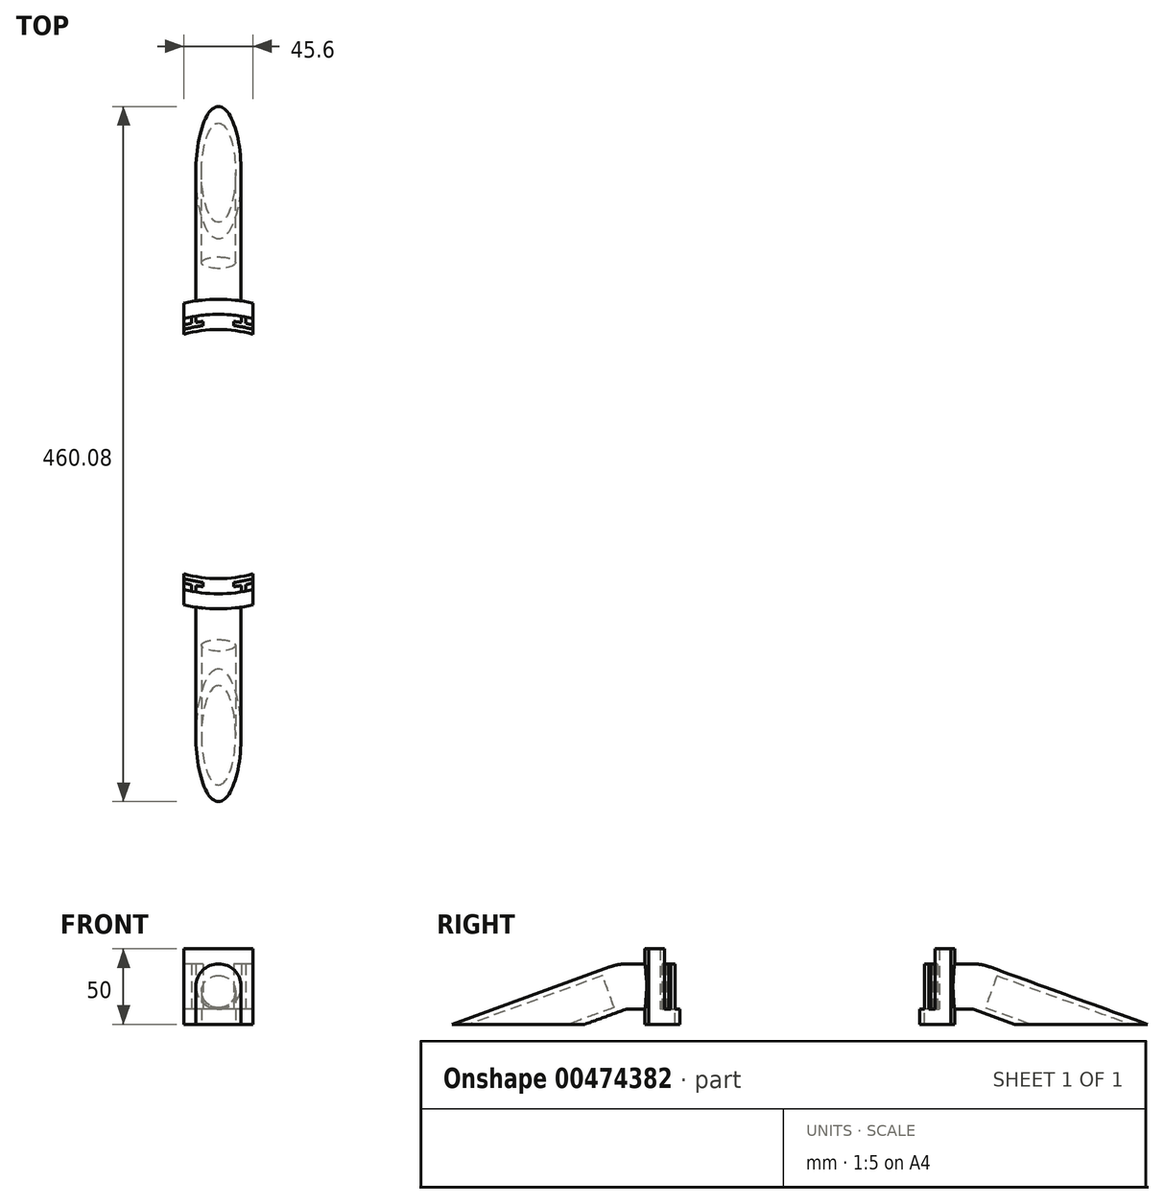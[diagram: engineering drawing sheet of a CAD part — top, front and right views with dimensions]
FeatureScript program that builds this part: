
annotation { "Feature Type Name" : "Feature", "Feature Type Description" : "" }
export const myFeature = defineFeature(function(context is Context, id is Id, definition is map)
    precondition{}
    {
        {
            var Q0;
            Q0=qCreatedBy(makeId("Top.planeOp"),FACE);
            var sketch = newSketch(context, id + "F0", { "sketchPlane" : qUnion([Q0])});
            skArc(sketch, "E0", {"start": v(-15.1, 91.26) * mm, "mid": v(-16.5, 91.02) * mm, "end": v(-17.9, 90.75) * mm});
            skCircle(sketch, "E1", {"center": v(0, 0) * mm, "radius": 82.5 * mm, "construction": true});
            skLineSegment(sketch, "E2", {"start": v(0, 0) * mm, "end": v(0, 99.1) * mm, "construction": true});
            skArc(sketch, "E3", {"start": v(-17.9, 86.57) * mm, "mid": v(-20.36, 86.02) * mm, "end": v(-22.8, 85.4) * mm});
            skArc(sketch, "E4", {"start": v(-10.2, 85) * mm, "mid": v(-16.54, 83.99) * mm, "end": v(-22.8, 82.5) * mm});
            skLineSegment(sketch, "E5", {"start": v(-15.1, 87.1) * mm, "end": v(-15.1, 91.26) * mm});
            skLineSegment(sketch, "E6", {"start": v(-17.9, 86.57) * mm, "end": v(-17.9, 90.75) * mm});
            skLineSegment(sketch, "E7", {"start": v(-10.2, 87.8) * mm, "end": v(-10.2, 85) * mm});
            skLineSegment(sketch, "E8", {"start": v(-22.8, 85.4) * mm, "end": v(-22.8, 82.5) * mm});
            skLineSegment(sketch, "E9.MirrorCS", {"start": v(10.2, 87.8) * mm, "end": v(10.2, 85) * mm});
            skLineSegment(sketch, "E10.MirrorCS", {"start": v(15.1, 87.1) * mm, "end": v(15.1, 91.26) * mm});
            skLineSegment(sketch, "E11.MirrorCS", {"start": v(17.9, 86.57) * mm, "end": v(17.9, 90.75) * mm});
            skLineSegment(sketch, "E12.MirrorCS", {"start": v(22.8, 85.4) * mm, "end": v(22.8, 82.5) * mm});
            skArc(sketch, "E13.trimOffspring", {"start": v(-10.2, 87.8) * mm, "mid": v(-12.65, 87.49) * mm, "end": v(-15.1, 87.1) * mm});
            skArc(sketch, "E14.trimOffspring", {"start": v(15.1, 87.1) * mm, "mid": v(12.65, 87.49) * mm, "end": v(10.2, 87.8) * mm});
            skArc(sketch, "E15.trimOffspring", {"start": v(17.9, 90.75) * mm, "mid": v(16.5, 91.02) * mm, "end": v(15.1, 91.26) * mm});
            skArc(sketch, "E16.trimOffspring", {"start": v(22.8, 82.5) * mm, "mid": v(16.54, 83.99) * mm, "end": v(10.2, 85) * mm});
            skArc(sketch, "E17.trimOffspring", {"start": v(22.8, 85.4) * mm, "mid": v(20.36, 86.02) * mm, "end": v(17.9, 86.57) * mm});
            skLineSegment(sketch, "E18", {"start": v(-16.5, 91.02) * mm, "end": v(-16.5, 84) * mm, "construction": true});
            skLineSegment(sketch, "E19", {"start": v(16.5, 91.02) * mm, "end": v(16.5, 84) * mm, "construction": true});
            skArc(sketch, "E20.1.0", {"start": v(10.2, -85) * mm, "mid": v(16.54, -83.99) * mm, "end": v(22.8, -82.5) * mm});
            skLineSegment(sketch, "E20.1.1", {"start": v(22.8, -85.4) * mm, "end": v(22.8, -82.5) * mm});
            skArc(sketch, "E20.1.2", {"start": v(17.9, -86.57) * mm, "mid": v(20.36, -86.02) * mm, "end": v(22.8, -85.4) * mm});
            skLineSegment(sketch, "E20.1.3", {"start": v(17.9, -86.57) * mm, "end": v(17.9, -90.75) * mm});
            skArc(sketch, "E20.1.4", {"start": v(15.1, -91.26) * mm, "mid": v(16.5, -91.02) * mm, "end": v(17.9, -90.75) * mm});
            skLineSegment(sketch, "E20.1.5", {"start": v(15.1, -87.1) * mm, "end": v(15.1, -91.26) * mm});
            skArc(sketch, "E20.1.6", {"start": v(10.2, -87.8) * mm, "mid": v(12.65, -87.49) * mm, "end": v(15.1, -87.1) * mm});
            skLineSegment(sketch, "E20.1.7", {"start": v(10.2, -87.8) * mm, "end": v(10.2, -85) * mm});
            skArc(sketch, "E20.1.8", {"start": v(-22.8, -82.5) * mm, "mid": v(-16.54, -83.99) * mm, "end": v(-10.2, -85) * mm});
            skLineSegment(sketch, "E20.1.9", {"start": v(-10.2, -87.8) * mm, "end": v(-10.2, -85) * mm});
            skArc(sketch, "E20.1.10", {"start": v(-15.1, -87.1) * mm, "mid": v(-12.65, -87.49) * mm, "end": v(-10.2, -87.8) * mm});
            skLineSegment(sketch, "E20.1.11", {"start": v(-15.1, -87.1) * mm, "end": v(-15.1, -91.26) * mm});
            skArc(sketch, "E20.1.12", {"start": v(-17.9, -90.75) * mm, "mid": v(-16.5, -91.02) * mm, "end": v(-15.1, -91.26) * mm});
            skLineSegment(sketch, "E20.1.13", {"start": v(-17.9, -86.57) * mm, "end": v(-17.9, -90.75) * mm});
            skArc(sketch, "E20.1.14", {"start": v(-22.8, -85.4) * mm, "mid": v(-20.36, -86.02) * mm, "end": v(-17.9, -86.57) * mm});
            skLineSegment(sketch, "E20.1.15", {"start": v(-22.8, -85.4) * mm, "end": v(-22.8, -82.5) * mm});
            skSolve(sketch);
        }
        {
            var Q0;
            Q0 = qSketchRegion(id + "F0", true);
            extrude(context, id + "F1", {"entities" : qUnion([Q0]), "depth" : 30 * mm});
        }
        {
            var Q0;
            Q0=qCreatedBy(makeId("Top.planeOp"),FACE);
            var sketch = newSketch(context, id + "F2", { "sketchPlane" : qUnion([Q0])});
            skArc(sketch, "E21", {"start": v(22.8, 89.65) * mm, "mid": v(0, 92.5) * mm, "end": v(-22.8, 89.65) * mm});
            skArc(sketch, "E22", {"start": v(22.8, 79.29) * mm, "mid": v(0, 82.5) * mm, "end": v(-22.8, 79.29) * mm});
            skArc(sketch, "E23.0.4", {"start": v(-15.1, 91.26) * mm, "mid": v(-16.5, 91.02) * mm, "end": v(-17.9, 90.75) * mm});
            skLineSegment(sketch, "E23.0.7", {"start": v(-22.8, 85.4) * mm, "end": v(-22.8, 82.5) * mm});
            skArc(sketch, "E24.0.2", {"start": v(17.9, 90.75) * mm, "mid": v(16.5, 91.02) * mm, "end": v(15.1, 91.26) * mm});
            skLineSegment(sketch, "E24.0.7", {"start": v(22.8, 82.5) * mm, "end": v(22.8, 85.4) * mm});
            skLineSegment(sketch, "E25", {"start": v(-22.8, 79.29) * mm, "end": v(-22.8, 89.65) * mm});
            skLineSegment(sketch, "E26", {"start": v(22.8, 79.29) * mm, "end": v(22.8, 89.65) * mm});
            skLineSegment(sketch, "E27.1.0", {"start": v(22.8, -79.29) * mm, "end": v(22.8, -89.65) * mm});
            skArc(sketch, "E27.1.1", {"start": v(-22.8, -79.29) * mm, "mid": v(0, -82.5) * mm, "end": v(22.8, -79.29) * mm});
            skArc(sketch, "E27.1.2", {"start": v(-22.8, -89.65) * mm, "mid": v(0, -92.5) * mm, "end": v(22.8, -89.65) * mm});
            skLineSegment(sketch, "E27.1.3", {"start": v(-22.8, -79.29) * mm, "end": v(-22.8, -89.65) * mm});
            skSolve(sketch);
        }
        {
            var Q0;
            Q0 = qSketchRegion(id + "F2", true);
            extrude(context, id + "F3", {"entities" : qUnion([Q0]), "operationType" : NewBodyOperationType.ADD, "oppositeDirection" : true, "depth" : 10 * mm});
        }
        {
            var Q0;
            Q0=qCreatedBy(makeId("Top.planeOp"),FACE);
            var sketch = newSketch(context, id + "F4", { "sketchPlane" : qUnion([Q0])});
            skArc(sketch, "E28.0.3", {"start": v(-22.8, 89.65) * mm, "mid": v(0, 92.5) * mm, "end": v(22.8, 89.65) * mm});
            skArc(sketch, "E29.0.2", {"start": v(22.8, -89.65) * mm, "mid": v(0, -92.5) * mm, "end": v(-22.8, -89.65) * mm});
            skArc(sketch, "E30", {"start": v(-22.8, -99.93) * mm, "mid": v(0, -102.5) * mm, "end": v(22.8, -99.93) * mm});
            skLineSegment(sketch, "E31", {"start": v(-22.8, -89.65) * mm, "end": v(-22.8, -99.93) * mm});
            skLineSegment(sketch, "E32", {"start": v(22.8, -89.65) * mm, "end": v(22.8, -99.93) * mm});
            skLineSegment(sketch, "E33", {"start": v(-22.8, 89.65) * mm, "end": v(-22.8, 99.93) * mm});
            skLineSegment(sketch, "E34", {"start": v(22.8, 89.65) * mm, "end": v(22.8, 99.93) * mm});
            skArc(sketch, "E35.trimOffspring", {"start": v(22.8, 99.93) * mm, "mid": v(0, 102.5) * mm, "end": v(-22.8, 99.93) * mm});
            skPoint(sketch, "E29.0.3.end.orphan", {"position": v(-22.8, -79.29) * mm});
            skPoint(sketch, "E29.0.1.start.orphan", {"position": v(22.8, -79.29) * mm});
            skPoint(sketch, "E28.0.1.start.orphan", {"position": v(22.8, 79.29) * mm});
            skPoint(sketch, "E28.0.2.start.orphan", {"position": v(-22.8, 79.29) * mm});
            skSolve(sketch);
        }
        {
            var Q0;
            Q0 = qSketchRegion(id + "F4", true);
            extrude(context, id + "F5", {"entities" : qUnion([Q0]), "operationType" : NewBodyOperationType.ADD, "depth" : 40 * mm, "hasSecondDirection" : true, "secondDirectionOppositeDirection" : true, "secondDirectionDepth" : 10 * mm});
        }
        {
            var Q0;
            Q0=qCreatedBy(makeId("Front.planeOp"),FACE);
            cPlane(context, id + "F6", {"entities" : qUnion([Q0]), "cplaneType" : CPlaneType.OFFSET, "offset" : 102.5 * mm, "width" : 150 * mm, "height" : 150 * mm});
        }
        {
            var Q0;
            Q0=qCreatedBy(id+"F6.planeOp",FACE);
            var sketch = newSketch(context, id + "F7", { "sketchPlane" : qUnion([Q0])});
            skCircle(sketch, "E36", {"center": v(0, 15) * mm, "radius": 15 * mm});
            skSolve(sketch);
        }
        {
            var Q0;
            Q0=qCreatedBy(makeId("Right.planeOp"),FACE);
            var sketch = newSketch(context, id + "F8", { "sketchPlane" : qUnion([Q0])});
            skPoint(sketch, "E37.0", {"position": v(-102.5, -10) * mm});
            skLineSegment(sketch, "E38", {"start": v(-120.81, 13.8) * mm, "end": v(-186.19, -10) * mm});
            skLineSegment(sketch, "E39.0.0", {"start": v(-102.5, 0) * mm, "end": v(-102.5, 30) * mm, "construction": true});
            skLineSegment(sketch, "E40", {"start": v(-113.97, 15) * mm, "end": v(-102.5, 15) * mm});
            skPoint(sketch, "E41.visualSharp", {"position": v(-117.5, 15) * mm});
            skArc(sketch, "E41.filletArc", {"start": v(-113.97, 15) * mm, "mid": v(-117.45, 14.7) * mm, "end": v(-120.81, 13.8) * mm});
            skLineSegment(sketch, "E42", {"start": v(-186.19, -10) * mm, "end": v(-191.32, 4.1) * mm, "construction": true});
            skLineSegment(sketch, "E43", {"start": v(-191.32, 4.1) * mm, "end": v(-230.04, -10) * mm, "construction": true});
            skLineSegment(sketch, "E44", {"start": v(-186.19, -10) * mm, "end": v(-230.04, -25.96) * mm});
            skSolve(sketch);
        }
        {
            var Q0;
            Q0 = qSketchRegion(id + "F7", true);
            var Q1;
            Q1=sQuery(id+"F8.wireOp",EDGE,"E40");
            var Q2;
            Q2=sQuery(id+"F8.wireOp",EDGE,"E41.filletArc");
            var Q3;
            Q3=sQuery(id+"F8.wireOp",EDGE,"E38");
            var Q4;
            Q4=sQuery(id+"F8.wireOp",EDGE,"E44");
            sweep(context, id + "F9", {"operationType" : NewBodyOperationType.ADD, "profiles" : qUnion([Q0]), "path" : qUnion([Q1, Q2, Q3, Q4])});
        }
        {
            var Q0;
            Q0=makeQuery(id+"F9.opSweep","CAP_FACE",FACE,{"disambiguationData":[OSD([sQuery(id+"F7.wireOp",EDGE,"E36"),sQuery(id+"F8.wireOp",VERTEX,"E44.end")])],"isStart":false});
            cPlane(context, id + "F10", {"entities" : qUnion([Q0]), "cplaneType" : CPlaneType.OFFSET, "offset" : 0 * mm, "width" : 150 * mm, "height" : 150 * mm});
        }
        {
            var Q0;
            Q0=qCreatedBy(id+"F10.planeOp",FACE);
            var sketch = newSketch(context, id + "F11", { "sketchPlane" : qUnion([Q0])});
            skCircle(sketch, "E45.0", {"center": v(0, 54.28) * mm, "radius": 15 * mm, "construction": true});
            skCircle(sketch, "E46", {"center": v(0, 54.28) * mm, "radius": 11.25 * mm});
            skSolve(sketch);
        }
        {
            var Q0;
            Q0 = qSketchRegion(id + "F11", true);
            var Q1;
            Q1=makeQuery(id+"F9.opSweep","SWEPT_FACE",FACE,{"disambiguationData":[OSD([sQuery(id+"F7.wireOp",EDGE,"E36"),sQuery(id+"F8.wireOp",EDGE,"E40")])]});
            extrude(context, id + "F12", {"entities" : qUnion([Q0]), "operationType" : NewBodyOperationType.REMOVE, "oppositeDirection" : true, "endBoundEntityFace" : qUnion([Q1]), "depth" : 110 * mm});
        }
        {
            var Q0;
            Q0 = qSketchRegion(id + "F7", true);
            var Q1;
            Q1=makeQuery(id+"F5.opExtrude","SWEPT_FACE",FACE,{"disambiguationData":[OSD([sQuery(id+"F4.wireOp",EDGE,"E30")])]});
            extrude(context, id + "F13", {"entities" : qUnion([Q0]), "operationType" : NewBodyOperationType.ADD, "endBound" : BoundingType.UP_TO_SURFACE, "oppositeDirection" : true, "endBoundEntityFace" : qUnion([Q1]), "depth" : 25 * mm, "hasSecondDirection" : true, "secondDirectionOppositeDirection" : false, "secondDirectionDepth" : 1 * mm});
        }
        {
            var Q0;
            Q0=qCreatedBy(makeId("Front.planeOp"),FACE);
            cPlane(context, id + "F14", {"entities" : qUnion([Q0]), "cplaneType" : CPlaneType.OFFSET, "offset" : 102.5 * mm, "oppositeDirection" : true, "width" : 150 * mm, "height" : 150 * mm});
        }
        {
            var Q0;
            Q0=qCreatedBy(id+"F14.planeOp",FACE);
            var sketch = newSketch(context, id + "F15", { "sketchPlane" : qUnion([Q0])});
            skCircle(sketch, "E47.0", {"center": v(0, 15) * mm, "radius": 15 * mm});
            skSolve(sketch);
        }
        {
            var Q0;
            Q0=qCreatedBy(makeId("Right.planeOp"),FACE);
            var sketch = newSketch(context, id + "F16", { "sketchPlane" : qUnion([Q0])});
            skLineSegment(sketch, "E48.0", {"start": v(102.5, 0) * mm, "end": v(102.5, 30) * mm, "construction": true});
            skLineSegment(sketch, "E49", {"start": v(-113.97, 30) * mm, "end": v(-102.5, 30) * mm, "construction": true});
            skLineSegment(sketch, "E50", {"start": v(-102.5, 0) * mm, "end": v(-113.97, 0) * mm, "construction": true});
            skArc(sketch, "E51", {"start": v(-113.97, 30) * mm, "mid": v(-120.05, 29.47) * mm, "end": v(-125.94, 27.89) * mm, "construction": true});
            skArc(sketch, "E52", {"start": v(-113.97, 0) * mm, "mid": v(-114.84, -0.08) * mm, "end": v(-115.68, -0.3) * mm, "construction": true});
            skLineSegment(sketch, "E53", {"start": v(-235.17, -11.87) * mm, "end": v(-125.94, 27.89) * mm, "construction": true});
            skLineSegment(sketch, "E54", {"start": v(-115.68, -0.3) * mm, "end": v(-224.91, -40.06) * mm, "construction": true});
            skLineSegment(sketch, "E55.MirrorCS", {"start": v(113.97, 30) * mm, "end": v(102.5, 30) * mm});
            skArc(sketch, "E56.MirrorCS", {"start": v(113.97, 30) * mm, "mid": v(120.05, 29.47) * mm, "end": v(125.94, 27.89) * mm});
            skLineSegment(sketch, "E57.MirrorCS", {"start": v(235.17, -11.87) * mm, "end": v(125.94, 27.89) * mm});
            skLineSegment(sketch, "E58.MirrorCS", {"start": v(115.68, -0.3) * mm, "end": v(224.91, -40.06) * mm, "construction": true});
            skLineSegment(sketch, "E59.MirrorCS", {"start": v(102.5, 0) * mm, "end": v(113.97, 0) * mm, "construction": true});
            skArc(sketch, "E60.MirrorCS", {"start": v(113.97, 0) * mm, "mid": v(114.84, -0.08) * mm, "end": v(115.68, -0.3) * mm, "construction": true});
            skSolve(sketch);
        }
        {
            var Q0;
            Q0 = qSketchRegion(id + "F15", true);
            var Q1;
            Q1=sQuery(id+"F16.wireOp",EDGE,"E55.MirrorCS");
            var Q2;
            Q2=sQuery(id+"F16.wireOp",EDGE,"E56.MirrorCS");
            var Q3;
            Q3=sQuery(id+"F16.wireOp",EDGE,"E57.MirrorCS");
            sweep(context, id + "F17", {"operationType" : NewBodyOperationType.ADD, "profiles" : qUnion([Q0]), "path" : qUnion([Q1, Q2, Q3])});
        }
        {
            var Q0;
            Q0 = qSketchRegion(id + "F15", true);
            extrude(context, id + "F18", {"entities" : qUnion([Q0]), "operationType" : NewBodyOperationType.ADD, "endBound" : BoundingType.UP_TO_NEXT, "depth" : 25 * mm, "hasSecondDirection" : true, "secondDirectionOppositeDirection" : true, "secondDirectionDepth" : 1 * mm});
        }
        {
            var Q0;
            Q0=makeQuery(id+"F17.opSweep","CAP_FACE",FACE,{"disambiguationData":[OSD([sQuery(id+"F15.wireOp",EDGE,"E47.0"),sQuery(id+"F16.wireOp",VERTEX,"E57.MirrorCS.start")])],"isStart":false});
            cPlane(context, id + "F19", {"entities" : qUnion([Q0]), "cplaneType" : CPlaneType.OFFSET, "offset" : 0 * mm, "width" : 150 * mm, "height" : 150 * mm});
        }
        {
            var Q0;
            Q0=qCreatedBy(id+"F19.planeOp",FACE);
            var sketch = newSketch(context, id + "F20", { "sketchPlane" : qUnion([Q0])});
            skCircle(sketch, "E61.0", {"center": v(0, 54.28) * mm, "radius": 15 * mm, "construction": true});
            skCircle(sketch, "E62", {"center": v(0, 54.28) * mm, "radius": 11.25 * mm});
            skSolve(sketch);
        }
        {
            var Q0;
            Q0 = qSketchRegion(id + "F20", true);
            extrude(context, id + "F21", {"entities" : qUnion([Q0]), "operationType" : NewBodyOperationType.REMOVE, "oppositeDirection" : true, "depth" : 110 * mm});
        }
        {
            var Q0;
            Q0=qCreatedBy(makeId("Right.planeOp"),FACE);
            var sketch = newSketch(context, id + "F22", { "sketchPlane" : qUnion([Q0])});
            skPoint(sketch, "E63.0", {"position": v(79.29, -10) * mm});
            skPoint(sketch, "E64.0", {"position": v(-79.29, -10) * mm});
            skLineSegment(sketch, "E65.bottom", {"start": v(79.29, -10) * mm, "end": v(248.01, -10) * mm});
            skLineSegment(sketch, "E65.top", {"start": v(79.29, -61.31) * mm, "end": v(248.01, -61.31) * mm});
            skLineSegment(sketch, "E65.left", {"start": v(79.29, -10) * mm, "end": v(79.29, -61.31) * mm});
            skLineSegment(sketch, "E65.right", {"start": v(248.01, -10) * mm, "end": v(248.01, -61.31) * mm});
            skLineSegment(sketch, "E66.bottom", {"start": v(-79.29, -10) * mm, "end": v(-247.55, -10) * mm});
            skLineSegment(sketch, "E66.top", {"start": v(-79.29, -65.45) * mm, "end": v(-247.55, -65.45) * mm});
            skLineSegment(sketch, "E66.left", {"start": v(-79.29, -10) * mm, "end": v(-79.29, -65.45) * mm});
            skLineSegment(sketch, "E66.right", {"start": v(-247.55, -10) * mm, "end": v(-247.55, -65.45) * mm});
            skSolve(sketch);
        }
        {
            var Q0;
            Q0 = qSketchRegion(id + "F22", true);
            extrude(context, id + "F23", {"entities" : qUnion([Q0]), "operationType" : NewBodyOperationType.REMOVE, "endBound" : BoundingType.THROUGH_ALL, "oppositeDirection" : true, "depth" : 25 * mm, "hasSecondDirection" : true, "secondDirectionBound" : SecondDirectionBoundingType.THROUGH_ALL, "secondDirectionOppositeDirection" : false, "secondDirectionDepth" : 25 * mm});
        }
    });
